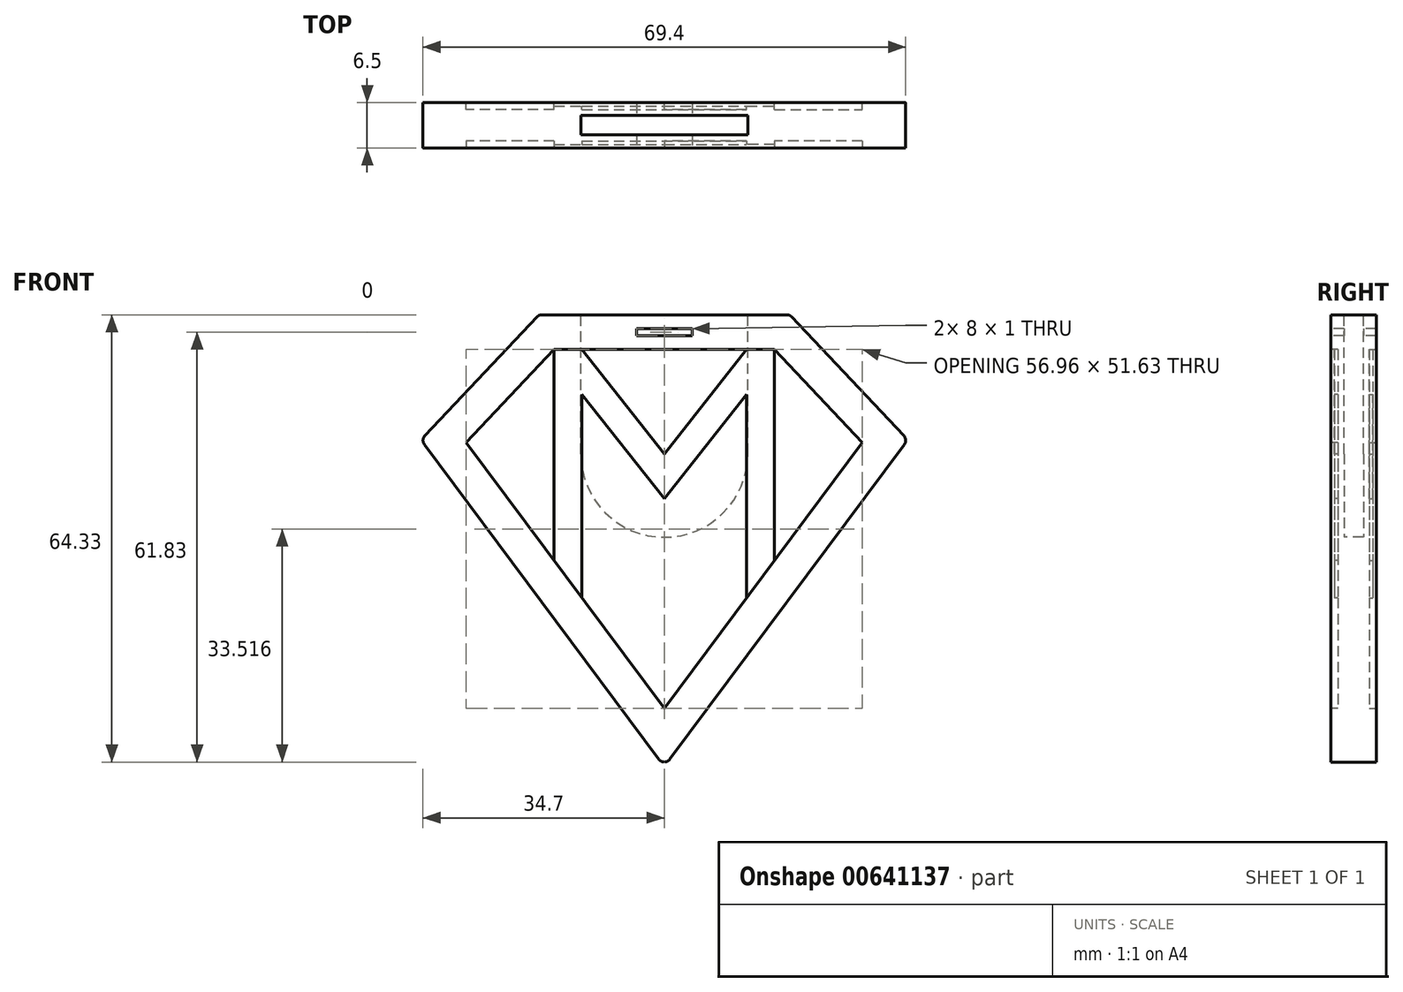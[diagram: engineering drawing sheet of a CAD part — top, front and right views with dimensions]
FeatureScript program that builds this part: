
annotation { "Feature Type Name" : "Feature", "Feature Type Description" : "" }
export const myFeature = defineFeature(function(context is Context, id is Id, definition is map)
    precondition{}
    {
        {
            var Q0;
            Q0=qCreatedBy(makeId("Front.planeOp"),FACE);
            var sketch = newSketch(context, id + "F0", { "sketchPlane" : qUnion([Q0])});
            skLineSegment(sketch, "E0", {"start": v(0, 18) * mm, "end": v(18, 18) * mm});
            skLineSegment(sketch, "E1", {"start": v(18, 18) * mm, "end": v(35, 0) * mm});
            skLineSegment(sketch, "E2", {"start": v(35, 0) * mm, "end": v(0, -47) * mm});
            skLineSegment(sketch, "E3", {"start": v(0, 18) * mm, "end": v(0, -47) * mm, "construction": true});
            skLineSegment(sketch, "E4.MirrorCS", {"start": v(-35, 0) * mm, "end": v(0, -47) * mm});
            skLineSegment(sketch, "E5.MirrorCS", {"start": v(-18, 18) * mm, "end": v(-35, 0) * mm});
            skLineSegment(sketch, "E6.MirrorCS", {"start": v(0, 18) * mm, "end": v(-18, 18) * mm});
            skSolve(sketch);
        }
        {
            var Q0;
            Q0=qSketchRegion(id+"F0",true);
            extrude(context, id + "F1", {"entities" : qUnion([Q0]), "endBound" : BoundingType.SYMMETRIC, "depth" : 6.5 * mm, "offsetDistance" : 25 * mm});
        }
        {
            var Q0;
            Q0=makeQuery(id+"F1.opExtrude","CAP_FACE",FACE,{"disambiguationData":[OSD([sQuery(id+"F0.wireOp",EDGE,"E0"),sQuery(id+"F0.wireOp",EDGE,"E1"),sQuery(id+"F0.wireOp",EDGE,"E2"),sQuery(id+"F0.wireOp",EDGE,"E4.MirrorCS"),sQuery(id+"F0.wireOp",EDGE,"E5.MirrorCS"),sQuery(id+"F0.wireOp",EDGE,"E6.MirrorCS")])],"isStart":false});
            var sketch = newSketch(context, id + "F2", { "sketchPlane" : qUnion([Q0])});
            skLineSegment(sketch, "E7.0", {"start": v(-15.84, 13) * mm, "end": v(15.84, 13) * mm});
            skLineSegment(sketch, "E8.0", {"start": v(-15.84, 13) * mm, "end": v(-28.48, -0.38) * mm});
            skLineSegment(sketch, "E9.0", {"start": v(-28.48, -0.38) * mm, "end": v(0, -38.63) * mm});
            skLineSegment(sketch, "E10.0", {"start": v(28.48, -0.38) * mm, "end": v(0, -38.63) * mm});
            skLineSegment(sketch, "E11.0", {"start": v(15.84, 13) * mm, "end": v(28.48, -0.38) * mm});
            skSolve(sketch);
        }
        {
            var Q0;
            Q0=qSketchRegion(id+"F2",true);
            extrude(context, id + "F3", {"entities" : qUnion([Q0]), "operationType" : NewBodyOperationType.REMOVE, "oppositeDirection" : true, "depth" : 0.5 * mm, "offsetDistance" : 25 * mm});
        }
        {
            var Q0;
            Q0=makeQuery(id+"F1.opExtrude","CAP_FACE",FACE,{"disambiguationData":[OSD([sQuery(id+"F0.wireOp",EDGE,"E0"),sQuery(id+"F0.wireOp",EDGE,"E1"),sQuery(id+"F0.wireOp",EDGE,"E2"),sQuery(id+"F0.wireOp",EDGE,"E4.MirrorCS"),sQuery(id+"F0.wireOp",EDGE,"E5.MirrorCS"),sQuery(id+"F0.wireOp",EDGE,"E6.MirrorCS")])],"isStart":true});
            var sketch = newSketch(context, id + "F4", { "sketchPlane" : qUnion([Q0])});
            skLineSegment(sketch, "E12.0", {"start": v(15.84, 13) * mm, "end": v(-15.84, 13) * mm});
            skLineSegment(sketch, "E13.0", {"start": v(15.84, 13) * mm, "end": v(28.48, -0.38) * mm});
            skLineSegment(sketch, "E14.0", {"start": v(28.48, -0.38) * mm, "end": v(0, -38.63) * mm});
            skLineSegment(sketch, "E15.0", {"start": v(-28.48, -0.38) * mm, "end": v(0, -38.63) * mm});
            skLineSegment(sketch, "E15.1", {"start": v(-15.84, 13) * mm, "end": v(-28.48, -0.38) * mm});
            skSolve(sketch);
        }
        {
            var Q0;
            Q0=qSketchRegion(id+"F4",true);
            extrude(context, id + "F5", {"entities" : qUnion([Q0]), "operationType" : NewBodyOperationType.REMOVE, "oppositeDirection" : true, "depth" : 0.5 * mm, "offsetDistance" : 25 * mm});
        }
        {
            var Q0;
            Q0=makeQuery(id+"F3.boolean.opBoolean","COPY",FACE,{"derivedFrom":makeQuery(id+"F3.opExtrude","CAP_FACE",FACE,{"disambiguationData":[OSD([sQuery(id+"F2.wireOp",EDGE,"E7.0"),sQuery(id+"F2.wireOp",EDGE,"E8.0"),sQuery(id+"F2.wireOp",EDGE,"E9.0"),sQuery(id+"F2.wireOp",EDGE,"E10.0"),sQuery(id+"F2.wireOp",EDGE,"E11.0")])],"isStart":false})});
            var sketch = newSketch(context, id + "F6", { "sketchPlane" : qUnion([Q0])});
            skLineSegment(sketch, "E16", {"start": v(-15.84, 13) * mm, "end": v(-15.84, -17.35) * mm});
            skLineSegment(sketch, "E17", {"start": v(15.84, 13) * mm, "end": v(15.84, -17.35) * mm});
            skLineSegment(sketch, "E18.0", {"start": v(-11.84, 6.55) * mm, "end": v(-11.84, -22.72) * mm});
            skLineSegment(sketch, "E19.0", {"start": v(11.84, 6.55) * mm, "end": v(11.84, -22.72) * mm});
            skLineSegment(sketch, "E20", {"start": v(-11.84, 13) * mm, "end": v(0, -2) * mm});
            skLineSegment(sketch, "E21", {"start": v(0, -2) * mm, "end": v(11.84, 13) * mm});
            skLineSegment(sketch, "E22.0", {"start": v(-11.84, 6.55) * mm, "end": v(0, -8.45) * mm});
            skLineSegment(sketch, "E23.0", {"start": v(0, -8.45) * mm, "end": v(11.84, 6.55) * mm});
            skPoint(sketch, "E24.0.start.orphan", {"position": v(-15.84, 13) * mm});
            skLineSegment(sketch, "E25", {"start": v(-11.84, 13) * mm, "end": v(11.84, 13) * mm});
            skLineSegment(sketch, "E26", {"start": v(-15.84, 13) * mm, "end": v(-28.48, -0.38) * mm});
            skLineSegment(sketch, "E27", {"start": v(-28.48, -0.38) * mm, "end": v(-15.84, -17.35) * mm});
            skLineSegment(sketch, "E28", {"start": v(0, -38.63) * mm, "end": v(11.84, -22.72) * mm});
            skLineSegment(sketch, "E29", {"start": v(28.48, -0.38) * mm, "end": v(15.84, 13) * mm});
            skLineSegment(sketch, "E30.trimOffspring", {"start": v(15.84, -17.35) * mm, "end": v(28.48, -0.38) * mm});
            skLineSegment(sketch, "E31.trimOffspring", {"start": v(-11.84, -22.72) * mm, "end": v(0, -38.63) * mm});
            skSolve(sketch);
        }
        {
            var Q0;
            Q0=qSketchRegion(id+"F6",true);
            extrude(context, id + "F7", {"entities" : qUnion([Q0]), "operationType" : NewBodyOperationType.REMOVE, "oppositeDirection" : true, "depth" : 0.5 * mm, "offsetDistance" : 25 * mm});
        }
        {
            var Q0;
            Q0=makeQuery(id+"F5.boolean.opBoolean","COPY",FACE,{"derivedFrom":makeQuery(id+"F5.opExtrude","CAP_FACE",FACE,{"disambiguationData":[OSD([sQuery(id+"F4.wireOp",EDGE,"E12.0"),sQuery(id+"F4.wireOp",EDGE,"E13.0"),sQuery(id+"F4.wireOp",EDGE,"E14.0"),sQuery(id+"F4.wireOp",EDGE,"E15.0"),sQuery(id+"F4.wireOp",EDGE,"E15.1")])],"isStart":false})});
            var sketch = newSketch(context, id + "F8", { "sketchPlane" : qUnion([Q0])});
            skLineSegment(sketch, "E32.0", {"start": v(-15.84, 13) * mm, "end": v(-15.84, -17.35) * mm});
            skLineSegment(sketch, "E32.1", {"start": v(-11.84, 6.55) * mm, "end": v(-11.84, -22.72) * mm});
            skLineSegment(sketch, "E32.2", {"start": v(0, -8.45) * mm, "end": v(-11.84, 6.55) * mm});
            skLineSegment(sketch, "E32.3", {"start": v(0, -2) * mm, "end": v(-11.84, 13) * mm});
            skLineSegment(sketch, "E32.4", {"start": v(11.84, 13) * mm, "end": v(0, -2) * mm});
            skLineSegment(sketch, "E32.5", {"start": v(11.84, 6.55) * mm, "end": v(0, -8.45) * mm});
            skLineSegment(sketch, "E32.6", {"start": v(11.84, 6.55) * mm, "end": v(11.84, -22.72) * mm});
            skLineSegment(sketch, "E32.7", {"start": v(15.84, 13) * mm, "end": v(15.84, -17.35) * mm});
            skLineSegment(sketch, "E32.8", {"start": v(15.84, 13) * mm, "end": v(28.48, -0.38) * mm});
            skLineSegment(sketch, "E32.9", {"start": v(28.48, -0.38) * mm, "end": v(15.84, -17.35) * mm});
            skLineSegment(sketch, "E32.10", {"start": v(-28.48, -0.38) * mm, "end": v(-15.84, -17.35) * mm});
            skLineSegment(sketch, "E32.11", {"start": v(-15.84, 13) * mm, "end": v(-28.48, -0.38) * mm});
            skLineSegment(sketch, "E32.12", {"start": v(11.84, 13) * mm, "end": v(-11.84, 13) * mm});
            skLineSegment(sketch, "E33.trimOffspring", {"start": v(11.84, -22.72) * mm, "end": v(0, -38.63) * mm});
            skLineSegment(sketch, "E34.trimOffspring", {"start": v(-11.84, -22.72) * mm, "end": v(0, -38.63) * mm});
            skSolve(sketch);
        }
        {
            var Q0;
            Q0=qSketchRegion(id+"F8",true);
            extrude(context, id + "F9", {"entities" : qUnion([Q0]), "operationType" : NewBodyOperationType.REMOVE, "oppositeDirection" : true, "depth" : 0.5 * mm, "offsetDistance" : 25 * mm});
        }
        {
            var Q0;
            Q0=makeQuery(id+"F1.opExtrude","SWEPT_FACE",FACE,{"disambiguationData":[OSD([sQuery(id+"F0.wireOp",EDGE,"E0"),sQuery(id+"F0.wireOp",EDGE,"E6.MirrorCS")])]});
            var sketch = newSketch(context, id + "F10", { "sketchPlane" : qUnion([Q0])});
            skLineSegment(sketch, "E35.bottom", {"start": v(-12, 1.4) * mm, "end": v(12, 1.4) * mm});
            skLineSegment(sketch, "E35.top", {"start": v(-12, -1.4) * mm, "end": v(12, -1.4) * mm});
            skLineSegment(sketch, "E35.left", {"start": v(-12, 1.4) * mm, "end": v(-12, -1.4) * mm});
            skLineSegment(sketch, "E35.right", {"start": v(12, 1.4) * mm, "end": v(12, -1.4) * mm});
            skSolve(sketch);
        }
        {
            var Q0;
            Q0=qSketchRegion(id+"F10",true);
            extrude(context, id + "F11", {"entities" : qUnion([Q0]), "operationType" : NewBodyOperationType.REMOVE, "oppositeDirection" : true, "depth" : 20 * mm, "offsetDistance" : 25 * mm});
        }
        {
            var Q0;
            Q0=qCreatedBy(makeId("Front.planeOp"),FACE);
            var sketch = newSketch(context, id + "F12", { "sketchPlane" : qUnion([Q0])});
            skLineSegment(sketch, "E36.0", {"start": v(-12, -2) * mm, "end": v(12, -2) * mm});
            skArc(sketch, "E37", {"start": v(-12, -2) * mm, "mid": v(0, -14) * mm, "end": v(12, -2) * mm});
            skSolve(sketch);
        }
        {
            var Q0;
            Q0=qSketchRegion(id+"F12",true);
            extrude(context, id + "F13", {"entities" : qUnion([Q0]), "operationType" : NewBodyOperationType.REMOVE, "endBound" : BoundingType.SYMMETRIC, "oppositeDirection" : true, "depth" : 2.8 * mm, "offsetDistance" : 25 * mm});
        }
        {
            var Q0;
            Q0=makeQuery(id+"F1.opExtrude","CAP_FACE",FACE,{"disambiguationData":[OSD([sQuery(id+"F0.wireOp",EDGE,"E0"),sQuery(id+"F0.wireOp",EDGE,"E1"),sQuery(id+"F0.wireOp",EDGE,"E2"),sQuery(id+"F0.wireOp",EDGE,"E4.MirrorCS"),sQuery(id+"F0.wireOp",EDGE,"E5.MirrorCS"),sQuery(id+"F0.wireOp",EDGE,"E6.MirrorCS")])],"isStart":false});
            var sketch = newSketch(context, id + "F14", { "sketchPlane" : qUnion([Q0])});
            skLineSegment(sketch, "E38.bottom", {"start": v(-4, 16) * mm, "end": v(4, 16) * mm});
            skLineSegment(sketch, "E38.top", {"start": v(-4, 15) * mm, "end": v(4, 15) * mm});
            skLineSegment(sketch, "E38.left", {"start": v(-4, 16) * mm, "end": v(-4, 15) * mm});
            skLineSegment(sketch, "E38.right", {"start": v(4, 16) * mm, "end": v(4, 15) * mm});
            skSolve(sketch);
        }
        {
            var Q0;
            Q0=qSketchRegion(id+"F14",true);
            extrude(context, id + "F15", {"entities" : qUnion([Q0]), "operationType" : NewBodyOperationType.REMOVE, "oppositeDirection" : true, "depth" : 25 * mm, "offsetDistance" : 25 * mm});
        }
        {
            var Q0;
            Q0=makeQuery(id+"F1.opExtrude","SWEPT_EDGE",EDGE,{"disambiguationData":[OSD([sQuery(id+"F0.wireOp",EDGE,"E2"),sQuery(id+"F0.wireOp",EDGE,"E4.MirrorCS")])]});
            var Q1;
            Q1=makeQuery(id+"F1.opExtrude","SWEPT_EDGE",EDGE,{"disambiguationData":[OSD([sQuery(id+"F0.wireOp",EDGE,"E1"),sQuery(id+"F0.wireOp",EDGE,"E2")])]});
            var Q2;
            Q2=makeQuery(id+"F1.opExtrude","SWEPT_EDGE",EDGE,{"disambiguationData":[OSD([sQuery(id+"F0.wireOp",EDGE,"E4.MirrorCS"),sQuery(id+"F0.wireOp",EDGE,"E5.MirrorCS")])]});
            var Q3;
            Q3=makeQuery(id+"F1.opExtrude","SWEPT_EDGE",EDGE,{"disambiguationData":[OSD([sQuery(id+"F0.wireOp",EDGE,"E5.MirrorCS"),sQuery(id+"F0.wireOp",EDGE,"E6.MirrorCS")])]});
            var Q4;
            Q4=makeQuery(id+"F1.opExtrude","SWEPT_EDGE",EDGE,{"disambiguationData":[OSD([sQuery(id+"F0.wireOp",EDGE,"E0"),sQuery(id+"F0.wireOp",EDGE,"E1")])]});
            fillet(context, id + "F16", {"entities" : qUnion([Q0, Q1, Q2, Q3, Q4]), "radius" : 1 * mm, "tangentPropagation" : true, "allowEdgeOverflow" : false});
        }
    });
